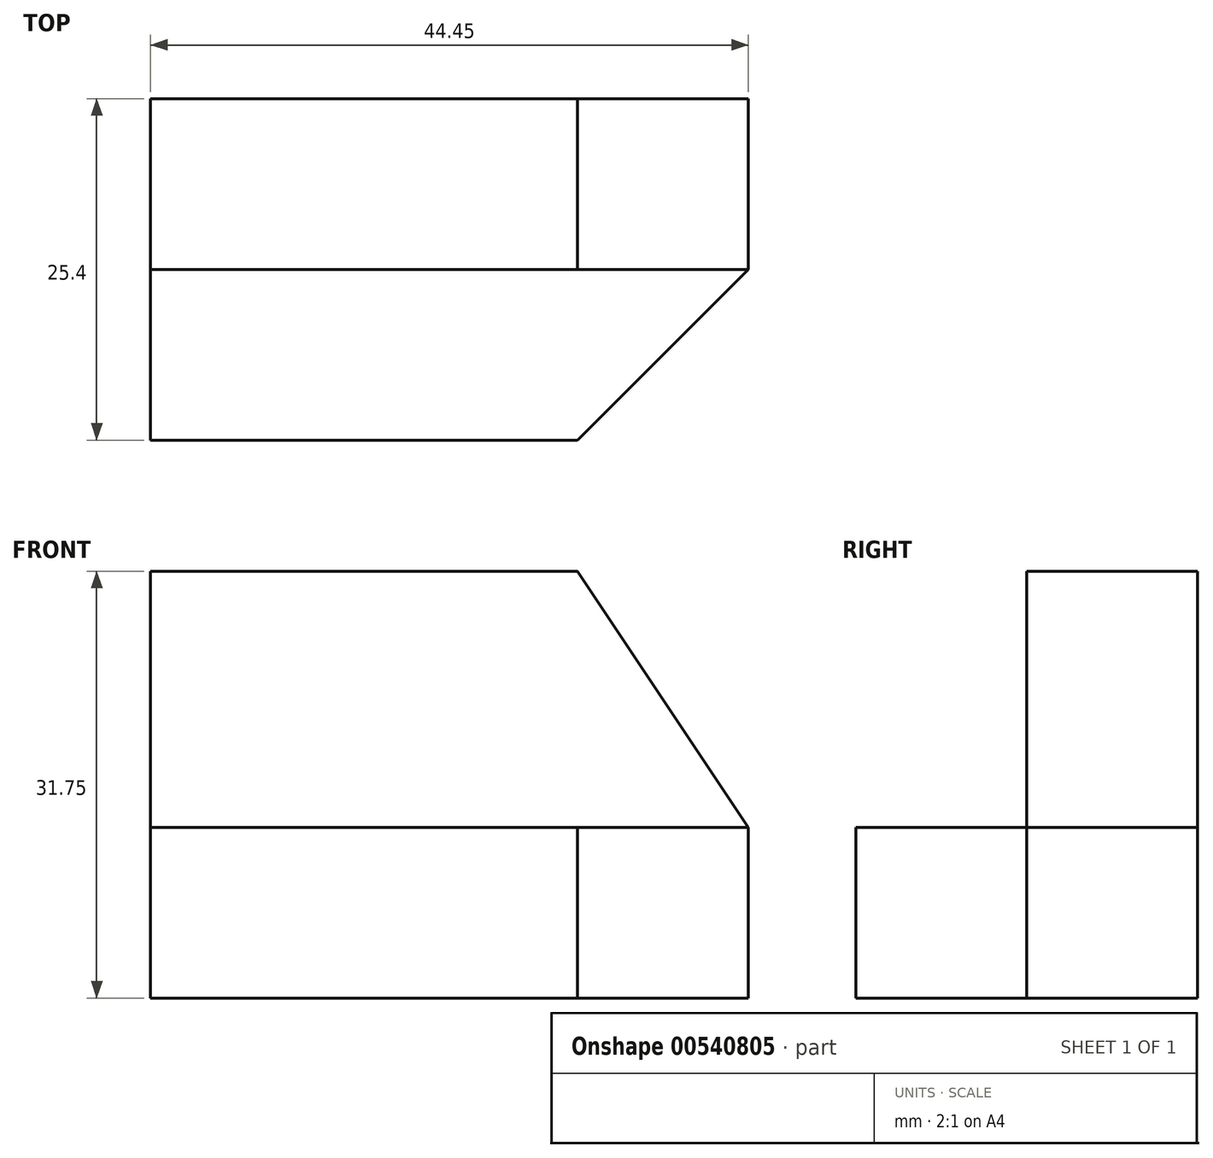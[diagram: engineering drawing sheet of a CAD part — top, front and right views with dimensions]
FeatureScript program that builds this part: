
annotation { "Feature Type Name" : "Feature", "Feature Type Description" : "" }
export const myFeature = defineFeature(function(context is Context, id is Id, definition is map)
    precondition{}
    {
        {
            var Q0;
            Q0=qCreatedBy(makeId("Front.planeOp"),FACE);
            var sketch = newSketch(context, id + "F0", { "sketchPlane" : qUnion([Q0])});
            skLineSegment(sketch, "E0", {"start": v(0, 0) * mm, "end": v(44.45, 0) * mm});
            skLineSegment(sketch, "E1", {"start": v(44.45, 0) * mm, "end": v(44.45, 31.75) * mm});
            skLineSegment(sketch, "E2", {"start": v(44.45, 31.75) * mm, "end": v(0, 31.75) * mm});
            skLineSegment(sketch, "E3", {"start": v(0, 31.75) * mm, "end": v(0, 0) * mm});
            skSolve(sketch);
        }
        {
            var Q0;
            Q0=makeQuery(id+"F0.imprint","IMPRINT",FACE,{"disambiguationData":[TD([[makeQuery(id+"F0.imprint","IMPRINT",EDGE,{"derivedFrom":sQuery(id+"F0.wireOp",EDGE,"E0")}),1.0]])]});
            extrude(context, id + "F1", {"entities" : qUnion([Q0]), "depth" : 25.4 * mm, "offsetDistance" : 25.4 * mm});
        }
        {
            var Q0;
            Q0=makeQuery(id+"F1.opExtrude","CAP_FACE",FACE,{"disambiguationData":[OSD([sQuery(id+"F0.wireOp",EDGE,"E0"),sQuery(id+"F0.wireOp",EDGE,"E1"),sQuery(id+"F0.wireOp",EDGE,"E2"),sQuery(id+"F0.wireOp",EDGE,"E3")])],"isStart":false});
            var sketch = newSketch(context, id + "F2", { "sketchPlane" : qUnion([Q0])});
            skLineSegment(sketch, "E4", {"start": v(0, 0) * mm, "end": v(0, 12.7) * mm});
            skLineSegment(sketch, "E5", {"start": v(0, 12.7) * mm, "end": v(44.45, 12.7) * mm});
            skLineSegment(sketch, "E6", {"start": v(44.45, 12.7) * mm, "end": v(44.45, 0) * mm});
            skLineSegment(sketch, "E7", {"start": v(44.45, 0) * mm, "end": v(0, 0) * mm});
            skSolve(sketch);
        }
        {
            var Q0;
            {var subQ0=sQuery(id+"F2.wireOp",EDGE,"E5");Q0=makeQuery(id+"F2.imprint","IMPRINT",FACE,{"disambiguationData":[TD([[makeQuery(id+"F2.imprint","IMPRINT",EDGE,{"derivedFrom":subQ0}),1.0]])]});}
            extrude(context, id + "F3", {"entities" : qUnion([Q0]), "operationType" : NewBodyOperationType.REMOVE, "oppositeDirection" : true, "depth" : 12.7 * mm, "offsetDistance" : 25.4 * mm});
        }
        {
            var Q0;
            Q0=makeQuery(id+"F3.boolean.opBoolean","COPY",FACE,{"derivedFrom":makeQuery(id+"F3.opExtrude","SWEPT_FACE",FACE,{"disambiguationData":[OSD([sQuery(id+"F2.wireOp",EDGE,"E5")])]})});
            var sketch = newSketch(context, id + "F4", { "sketchPlane" : qUnion([Q0])});
            skLineSegment(sketch, "E8", {"start": v(44.45, -12.7) * mm, "end": v(31.75, -25.4) * mm});
            skLineSegment(sketch, "E9", {"start": v(31.75, -25.4) * mm, "end": v(44.45, -25.4) * mm});
            skLineSegment(sketch, "E10", {"start": v(44.45, -25.4) * mm, "end": v(44.45, -12.7) * mm});
            skSolve(sketch);
        }
        {
            var Q0;
            Q0=makeQuery(id+"F4.imprint","IMPRINT",FACE,{"disambiguationData":[TD([[makeQuery(id+"F4.imprint","IMPRINT",EDGE,{"derivedFrom":sQuery(id+"F4.wireOp",EDGE,"E8")}),1.0]])]});
            extrude(context, id + "F5", {"entities" : qUnion([Q0]), "operationType" : NewBodyOperationType.REMOVE, "oppositeDirection" : true, "depth" : 25.4 * mm, "offsetDistance" : 25.4 * mm});
        }
        {
            var Q0;
            Q0=makeQuery(id+"F3.boolean.opBoolean","COPY",FACE,{"derivedFrom":makeQuery(id+"F3.opExtrude","CAP_FACE",FACE,{"disambiguationData":[OSD([sQuery(id+"F0.wireOp",EDGE,"E1"),sQuery(id+"F0.wireOp",EDGE,"E2"),sQuery(id+"F0.wireOp",EDGE,"E3"),sQuery(id+"F2.wireOp",EDGE,"E5")])],"isStart":false})});
            var sketch = newSketch(context, id + "F6", { "sketchPlane" : qUnion([Q0])});
            skLineSegment(sketch, "E11", {"start": v(44.45, 12.7) * mm, "end": v(31.75, 31.75) * mm});
            skLineSegment(sketch, "E12", {"start": v(31.75, 31.75) * mm, "end": v(44.45, 31.75) * mm});
            skLineSegment(sketch, "E13", {"start": v(44.45, 31.75) * mm, "end": v(44.45, 12.7) * mm});
            skSolve(sketch);
        }
        {
            var Q0;
            Q0=makeQuery(id+"F6.imprint","IMPRINT",FACE,{"disambiguationData":[TD([[makeQuery(id+"F6.imprint","IMPRINT",EDGE,{"derivedFrom":sQuery(id+"F6.wireOp",EDGE,"E11")}),-1.0]])]});
            extrude(context, id + "F7", {"entities" : qUnion([Q0]), "operationType" : NewBodyOperationType.REMOVE, "oppositeDirection" : true, "depth" : 25.4 * mm, "offsetDistance" : 25.4 * mm});
        }
    });
